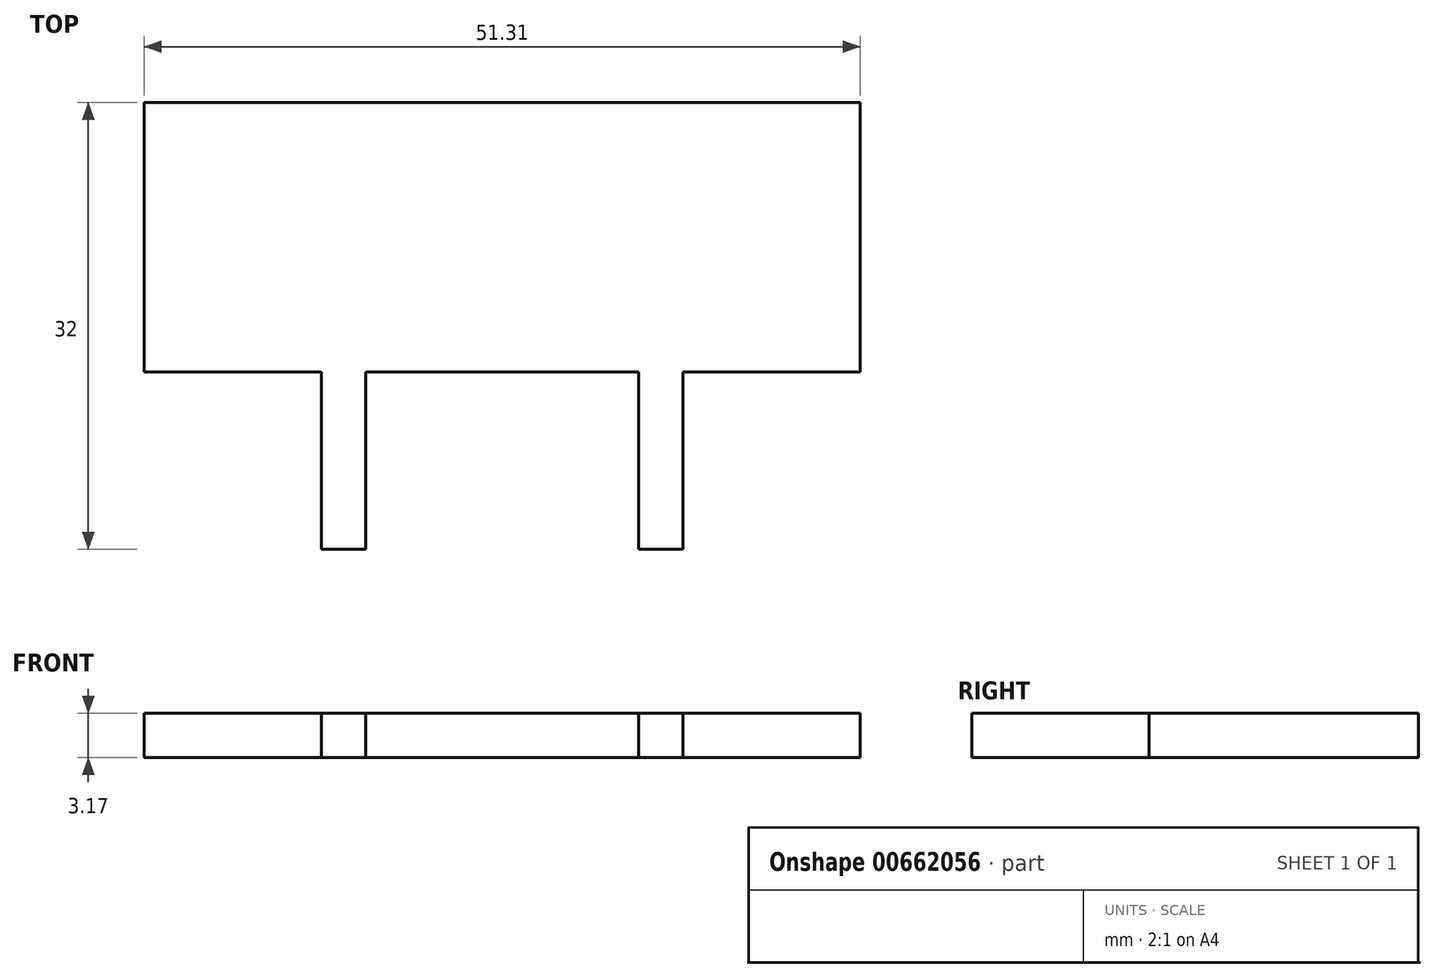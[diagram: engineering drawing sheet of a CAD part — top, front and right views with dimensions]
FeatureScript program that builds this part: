
annotation { "Feature Type Name" : "Feature", "Feature Type Description" : "" }
export const myFeature = defineFeature(function(context is Context, id is Id, definition is map)
    precondition{}
    {
        {
            var Q0;
            Q0=qCreatedBy(makeId("Top.planeOp"),FACE);
            var sketch = newSketch(context, id + "F0", { "sketchPlane" : qUnion([Q0])});
            skLineSegment(sketch, "E0.bottom", {"start": v(0, 0) * mm, "end": v(51.3, 0) * mm});
            skLineSegment(sketch, "E0.top", {"start": v(0, 19.3) * mm, "end": v(51.3, 19.3) * mm});
            skLineSegment(sketch, "E0.left", {"start": v(0, 0) * mm, "end": v(0, 19.3) * mm});
            skLineSegment(sketch, "E0.right", {"start": v(51.3, 0) * mm, "end": v(51.3, 19.3) * mm});
            skSolve(sketch);
        }
        {
            var Q0;
            Q0=makeQuery(id+"F0.imprint","IMPRINT",FACE,{"disambiguationData":[TD([[makeQuery(id+"F0.imprint","IMPRINT",EDGE,{"derivedFrom":sQuery(id+"F0.wireOp",EDGE,"E0.bottom")}),1.0]])]});
            extrude(context, id + "F1", {"entities" : qUnion([Q0]), "depth" : 3.17 * mm, "offsetDistance" : 25.4 * mm});
        }
        {
            var Q0;
            Q0=makeQuery(id+"F1.opExtrude","CAP_FACE",FACE,{"disambiguationData":[OSD([sQuery(id+"F0.wireOp",EDGE,"E0.bottom"),sQuery(id+"F0.wireOp",EDGE,"E0.top"),sQuery(id+"F0.wireOp",EDGE,"E0.left"),sQuery(id+"F0.wireOp",EDGE,"E0.right")])],"isStart":false});
            var sketch = newSketch(context, id + "F2", { "sketchPlane" : qUnion([Q0])});
            skLineSegment(sketch, "E1.bottom", {"start": v(35.43, 0) * mm, "end": v(38.6, 0) * mm});
            skLineSegment(sketch, "E1.top", {"start": v(35.43, -12.7) * mm, "end": v(38.6, -12.7) * mm});
            skLineSegment(sketch, "E1.left", {"start": v(35.43, 0) * mm, "end": v(35.43, -12.7) * mm});
            skLineSegment(sketch, "E1.right", {"start": v(38.6, 0) * mm, "end": v(38.6, -12.7) * mm});
            skLineSegment(sketch, "E2.bottom", {"start": v(12.7, 0) * mm, "end": v(15.88, 0) * mm});
            skLineSegment(sketch, "E2.top", {"start": v(12.7, -12.7) * mm, "end": v(15.88, -12.7) * mm});
            skLineSegment(sketch, "E2.left", {"start": v(12.7, 0) * mm, "end": v(12.7, -12.7) * mm});
            skLineSegment(sketch, "E2.right", {"start": v(15.88, 0) * mm, "end": v(15.88, -12.7) * mm});
            skSolve(sketch);
        }
        {
            var Q0;
            Q0 = qSketchRegion(id + "F2", true);
            extrude(context, id + "F3", {"entities" : qUnion([Q0]), "operationType" : NewBodyOperationType.ADD, "oppositeDirection" : true, "depth" : 3.17 * mm, "offsetDistance" : 25.4 * mm});
        }
    });
